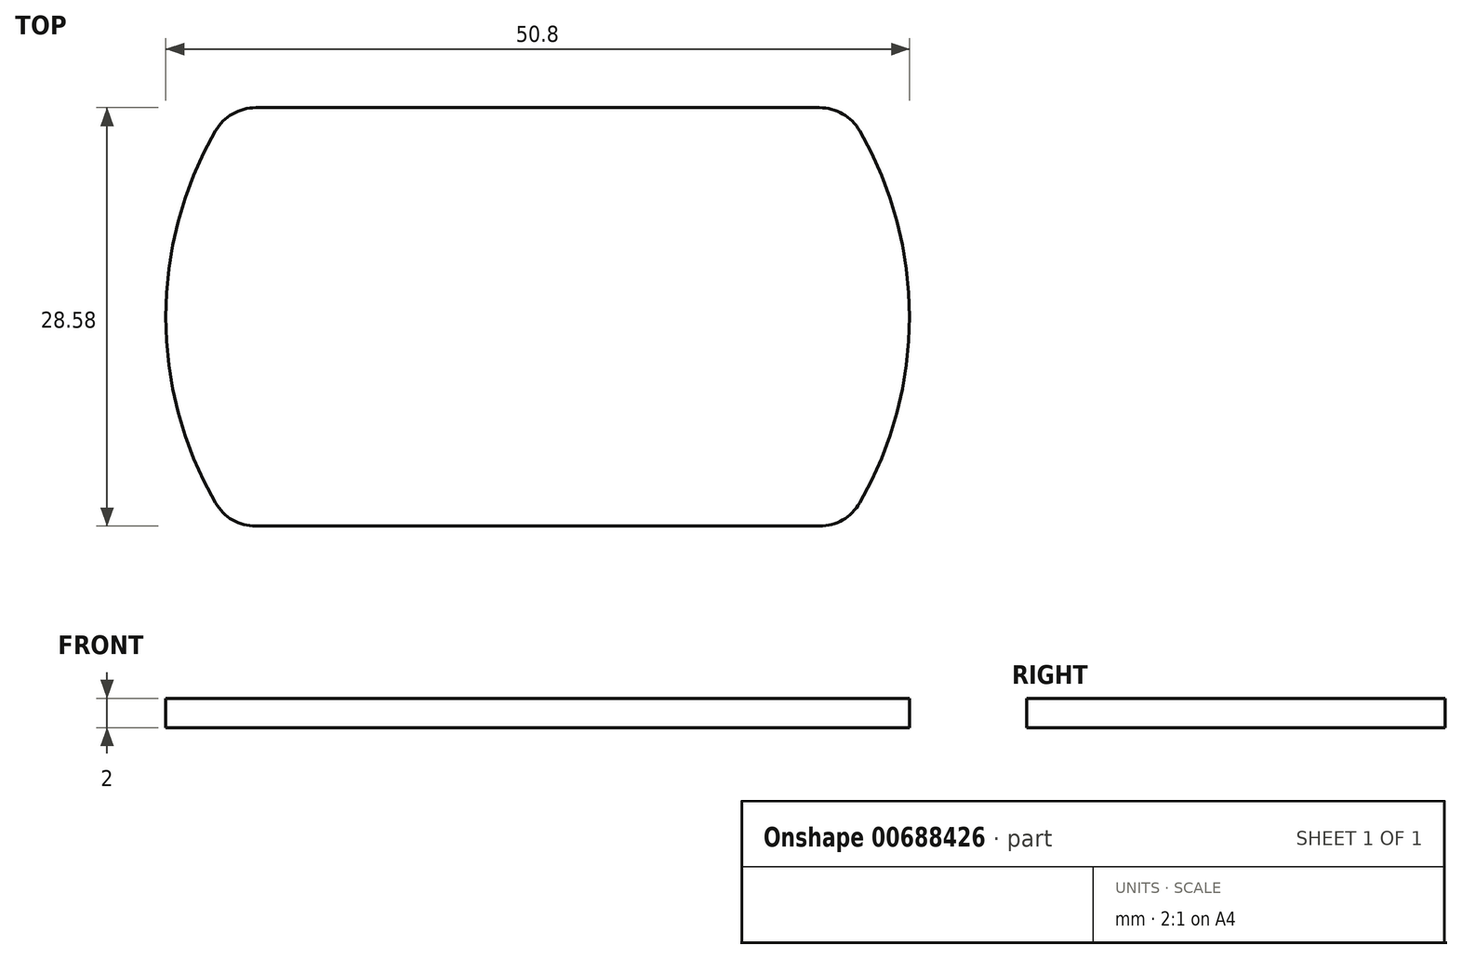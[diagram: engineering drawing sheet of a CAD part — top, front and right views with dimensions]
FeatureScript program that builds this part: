
annotation { "Feature Type Name" : "Feature", "Feature Type Description" : "" }
export const myFeature = defineFeature(function(context is Context, id is Id, definition is map)
    precondition{}
    {
        {
            var Q0;
            Q0=qCreatedBy(makeId("Top.planeOp"),FACE);
            var sketch = newSketch(context, id + "F0", { "sketchPlane" : qUnion([Q0])});
            skArc(sketch, "E0", {"start": v(-22, 12.7) * mm, "mid": v(-25.4, 0) * mm, "end": v(-22, -12.7) * mm});
            skLineSegment(sketch, "E1.top", {"start": v(-19.25, -14.29) * mm, "end": v(19.25, -14.29) * mm});
            skArc(sketch, "E2.trimOffspring", {"start": v(22, -12.7) * mm, "mid": v(25.4, 0) * mm, "end": v(22, 12.7) * mm});
            skLineSegment(sketch, "E3", {"start": v(-19.25, 14.29) * mm, "end": v(19.25, 14.29) * mm});
            skPoint(sketch, "E4.visualSharp", {"position": v(-21, 14.29) * mm});
            skArc(sketch, "E4.filletArc", {"start": v(-19.25, 14.29) * mm, "mid": v(-20.83, 13.86) * mm, "end": v(-22, 12.7) * mm});
            skPoint(sketch, "E5.visualSharp", {"position": v(21, 14.29) * mm});
            skArc(sketch, "E5.filletArc", {"start": v(22, 12.7) * mm, "mid": v(20.83, 13.86) * mm, "end": v(19.25, 14.29) * mm});
            skPoint(sketch, "E6.visualSharp", {"position": v(21, -14.29) * mm});
            skArc(sketch, "E6.filletArc", {"start": v(19.25, -14.29) * mm, "mid": v(20.83, -13.86) * mm, "end": v(22, -12.7) * mm});
            skPoint(sketch, "E7.visualSharp", {"position": v(-21, -14.29) * mm});
            skArc(sketch, "E7.filletArc", {"start": v(-22, -12.7) * mm, "mid": v(-20.83, -13.86) * mm, "end": v(-19.25, -14.29) * mm});
            skSolve(sketch);
        }
        {
            var Q0;
            Q0=makeQuery(id+"F0.imprint","IMPRINT",FACE,{"disambiguationData":[TD([[makeQuery(id+"F0.imprint","IMPRINT",EDGE,{"derivedFrom":sQuery(id+"F0.wireOp",EDGE,"E0")}),1.0]])]});
            extrude(context, id + "F1", {"entities" : qUnion([Q0]), "depth" : 1 * mm, "offsetDistance" : 25.4 * mm});
        }
        {
            var Q0;
            Q0=makeQuery(id+"F1.opExtrude","CAP_FACE",FACE,{"disambiguationData":[OSD([sQuery(id+"F0.wireOp",EDGE,"E0"),sQuery(id+"F0.wireOp",EDGE,"E1.top"),sQuery(id+"F0.wireOp",EDGE,"E2.trimOffspring"),sQuery(id+"F0.wireOp",EDGE,"E3"),sQuery(id+"F0.wireOp",EDGE,"E4.filletArc"),sQuery(id+"F0.wireOp",EDGE,"E5.filletArc"),sQuery(id+"F0.wireOp",EDGE,"E6.filletArc"),sQuery(id+"F0.wireOp",EDGE,"E7.filletArc")])],"isStart":false});
            var sketch = newSketch(context, id + "F2", { "sketchPlane" : qUnion([Q0])});
            skLineSegment(sketch, "E8.0", {"start": v(-18.66, 13.29) * mm, "end": v(18.66, 13.29) * mm});
            skArc(sketch, "E8.1", {"start": v(-21.45, 11.63) * mm, "mid": v(-24.4, 0) * mm, "end": v(-21.45, -11.63) * mm});
            skLineSegment(sketch, "E8.2", {"start": v(-18.66, -13.29) * mm, "end": v(18.66, -13.29) * mm});
            skArc(sketch, "E8.3", {"start": v(21.45, -11.63) * mm, "mid": v(24.4, 0) * mm, "end": v(21.45, 11.63) * mm});
            skPoint(sketch, "E9.visualSharp", {"position": v(-20.46, 13.29) * mm});
            skArc(sketch, "E9.filletArc", {"start": v(-18.66, 13.29) * mm, "mid": v(-20.29, 12.84) * mm, "end": v(-21.45, 11.63) * mm});
            skPoint(sketch, "E10.visualSharp", {"position": v(20.46, 13.29) * mm});
            skArc(sketch, "E10.filletArc", {"start": v(21.45, 11.63) * mm, "mid": v(20.29, 12.84) * mm, "end": v(18.66, 13.29) * mm});
            skPoint(sketch, "E11.visualSharp", {"position": v(20.46, -13.29) * mm});
            skArc(sketch, "E11.filletArc", {"start": v(18.66, -13.29) * mm, "mid": v(20.29, -12.84) * mm, "end": v(21.45, -11.63) * mm});
            skPoint(sketch, "E12.visualSharp", {"position": v(-20.46, -13.29) * mm});
            skArc(sketch, "E12.filletArc", {"start": v(-21.45, -11.63) * mm, "mid": v(-20.29, -12.84) * mm, "end": v(-18.66, -13.29) * mm});
            skLineSegment(sketch, "E13.0", {"start": v(-19.25, 14.29) * mm, "end": v(19.25, 14.29) * mm});
            skArc(sketch, "E13.1", {"start": v(-22, 12.7) * mm, "mid": v(-25.4, 0) * mm, "end": v(-22, -12.7) * mm});
            skLineSegment(sketch, "E13.2", {"start": v(-19.25, -14.29) * mm, "end": v(19.25, -14.29) * mm});
            skArc(sketch, "E13.3", {"start": v(22, -12.7) * mm, "mid": v(25.4, 0) * mm, "end": v(22, 12.7) * mm});
            skPoint(sketch, "E14.visualSharp", {"position": v(-21, -14.29) * mm});
            skArc(sketch, "E14.filletArc", {"start": v(-22, -12.7) * mm, "mid": v(-20.83, -13.86) * mm, "end": v(-19.25, -14.29) * mm});
            skPoint(sketch, "E15.visualSharp", {"position": v(21, -14.29) * mm});
            skArc(sketch, "E15.filletArc", {"start": v(19.25, -14.29) * mm, "mid": v(20.83, -13.86) * mm, "end": v(22, -12.7) * mm});
            skPoint(sketch, "E16.visualSharp", {"position": v(21, 14.29) * mm});
            skArc(sketch, "E16.filletArc", {"start": v(22, 12.7) * mm, "mid": v(20.83, 13.86) * mm, "end": v(19.25, 14.29) * mm});
            skPoint(sketch, "E17.visualSharp", {"position": v(-21, 14.29) * mm});
            skArc(sketch, "E17.filletArc", {"start": v(-19.25, 14.29) * mm, "mid": v(-20.83, 13.86) * mm, "end": v(-22, 12.7) * mm});
            skSolve(sketch);
        }
        {
            var Q0;
            Q0=makeQuery(id+"F2.imprint","IMPRINT",FACE,{"disambiguationData":[TD([[makeQuery(id+"F2.imprint","IMPRINT",EDGE,{"derivedFrom":sQuery(id+"F2.wireOp",EDGE,"E8.0")}),1.0]])]});
            extrude(context, id + "F3", {"entities" : qUnion([Q0]), "operationType" : NewBodyOperationType.ADD, "depth" : 1 * mm, "offsetDistance" : 25.4 * mm});
        }
        {
            var Q0;
            Q0=makeQuery(id+"F1.opExtrude","CAP_FACE",FACE,{"disambiguationData":[OSD([sQuery(id+"F0.wireOp",EDGE,"E0"),sQuery(id+"F0.wireOp",EDGE,"E1.top"),sQuery(id+"F0.wireOp",EDGE,"E2.trimOffspring"),sQuery(id+"F0.wireOp",EDGE,"E3"),sQuery(id+"F0.wireOp",EDGE,"E4.filletArc"),sQuery(id+"F0.wireOp",EDGE,"E5.filletArc"),sQuery(id+"F0.wireOp",EDGE,"E6.filletArc"),sQuery(id+"F0.wireOp",EDGE,"E7.filletArc")])],"isStart":false});
            var sketch = newSketch(context, id + "F4", { "sketchPlane" : qUnion([Q0])});
            skCircle(sketch, "E18", {"center": v(-21.82, 0) * mm, "radius": 1.59 * mm});
            skSolve(sketch);
        }
        {
            var Q0;
            Q0=makeQuery(id+"F4.imprint","IMPRINT",FACE,{"disambiguationData":[TD([[makeQuery(id+"F4.imprint","IMPRINT",EDGE,{"derivedFrom":sQuery(id+"F4.wireOp",EDGE,"E18")}),1.0]])]});
            extrude(context, id + "F5", {"entities" : qUnion([Q0]), "operationType" : NewBodyOperationType.REMOVE, "oppositeDirection" : true, "depth" : 1 * mm, "offsetDistance" : 25.4 * mm});
        }
        {
            var Q0;
            Q0=makeQuery(id+"F2.imprint","IMPRINT",FACE,{"disambiguationData":[TD([[makeQuery(id+"F2.imprint","IMPRINT",EDGE,{"derivedFrom":sQuery(id+"F2.wireOp",EDGE,"E8.0")}),-1.0]])]});
            var sketch = newSketch(context, id + "F6", { "sketchPlane" : qUnion([Q0])});
            skText(sketch, "E19", { "text": "clifton", "fontName": "OpenSans-Italic.ttf"});
            const initialGuessF6  = {"E19": [-0.01763, 0, 1, 0, 0.01005]};
            skSetInitialGuess(sketch, initialGuessF6);
            skSolve(sketch);
        }
        {
            var Q0;
            Q0 = qSketchRegion(id + "F6", true);
            extrude(context, id + "F7", {"entities" : qUnion([Q0]), "operationType" : NewBodyOperationType.ADD, "depth" : 1 * mm, "offsetDistance" : 25.4 * mm});
        }
        {
            var Q0;
            Q0=makeQuery(id+"F2.imprint","IMPRINT",FACE,{"disambiguationData":[TD([[makeQuery(id+"F2.imprint","IMPRINT",EDGE,{"derivedFrom":sQuery(id+"F2.wireOp",EDGE,"E8.0")}),-1.0]])]});
            var sketch = newSketch(context, id + "F8", { "sketchPlane" : qUnion([Q0])});
            skText(sketch, "E20", { "text": "fuller", "fontName": "OpenSans-Italic.ttf"});
            const initialGuessF8  = {"E20": [-0.01196, -0.0113, 1, 0, 0.0069]};
            skSetInitialGuess(sketch, initialGuessF8);
            skSolve(sketch);
        }
        {
            var Q0;
            Q0 = qSketchRegion(id + "F8", true);
            extrude(context, id + "F9", {"entities" : qUnion([Q0]), "operationType" : NewBodyOperationType.ADD, "depth" : 1 * mm, "offsetDistance" : 25.4 * mm});
        }
        {
            var Q0;
            Q0=makeQuery(id+"F2.imprint","IMPRINT",FACE,{"disambiguationData":[TD([[makeQuery(id+"F2.imprint","IMPRINT",EDGE,{"derivedFrom":sQuery(id+"F2.wireOp",EDGE,"E8.0")}),-1.0]])]});
            extrude(context, id + "F10", {"entities" : qUnion([Q0]), "operationType" : NewBodyOperationType.ADD, "depth" : 1 * mm, "offsetDistance" : 25.4 * mm});
        }
        {
            var Q0;
            Q0 = qSketchRegion(id + "F8", true);
            var Q1;
            Q1=makeQuery(id+"F0.imprint","IMPRINT",FACE,{"disambiguationData":[TD([[makeQuery(id+"F0.imprint","IMPRINT",EDGE,{"derivedFrom":sQuery(id+"F0.wireOp",EDGE,"E0")}),1.0]])]});
            var Q2;
            Q2 = qSketchRegion(id + "F6", true);
            extrude(context, id + "F11", {"entities" : qUnion([Q0, Q1, Q2]), "operationType" : NewBodyOperationType.ADD, "depth" : 1 * mm, "offsetDistance" : 25.4 * mm});
        }
        {
            var Q0;
            Q0 = qSketchRegion(id + "F6", true);
            var Q1;
            Q1 = qSketchRegion(id + "F8", true);
            extrude(context, id + "F12", {"entities" : qUnion([Q0, Q1]), "operationType" : NewBodyOperationType.ADD, "depth" : 1 * mm, "offsetDistance" : 25.4 * mm});
        }
        {
            var Q0;
            Q0 = qSketchRegion(id + "F6", true);
            extrude(context, id + "F13", {"entities" : qUnion([Q0]), "operationType" : NewBodyOperationType.ADD, "depth" : 1 * mm, "offsetDistance" : 25.4 * mm});
        }
        {
            var Q0;
            Q0 = qSketchRegion(id + "F6", true);
            var Q1;
            Q1 = qSketchRegion(id + "F8", true);
            extrude(context, id + "F14", {"entities" : qUnion([Q0, Q1]), "operationType" : NewBodyOperationType.ADD, "depth" : 1 * mm, "offsetDistance" : 25.4 * mm});
        }
        {
            var Q0;
            Q0 = qSketchRegion(id + "F6", true);
            var Q1;
            Q1 = qSketchRegion(id + "F8", true);
            extrude(context, id + "F15", {"entities" : qUnion([Q0, Q1]), "operationType" : NewBodyOperationType.ADD, "depth" : 1 * mm, "offsetDistance" : 25.4 * mm});
        }
    });
